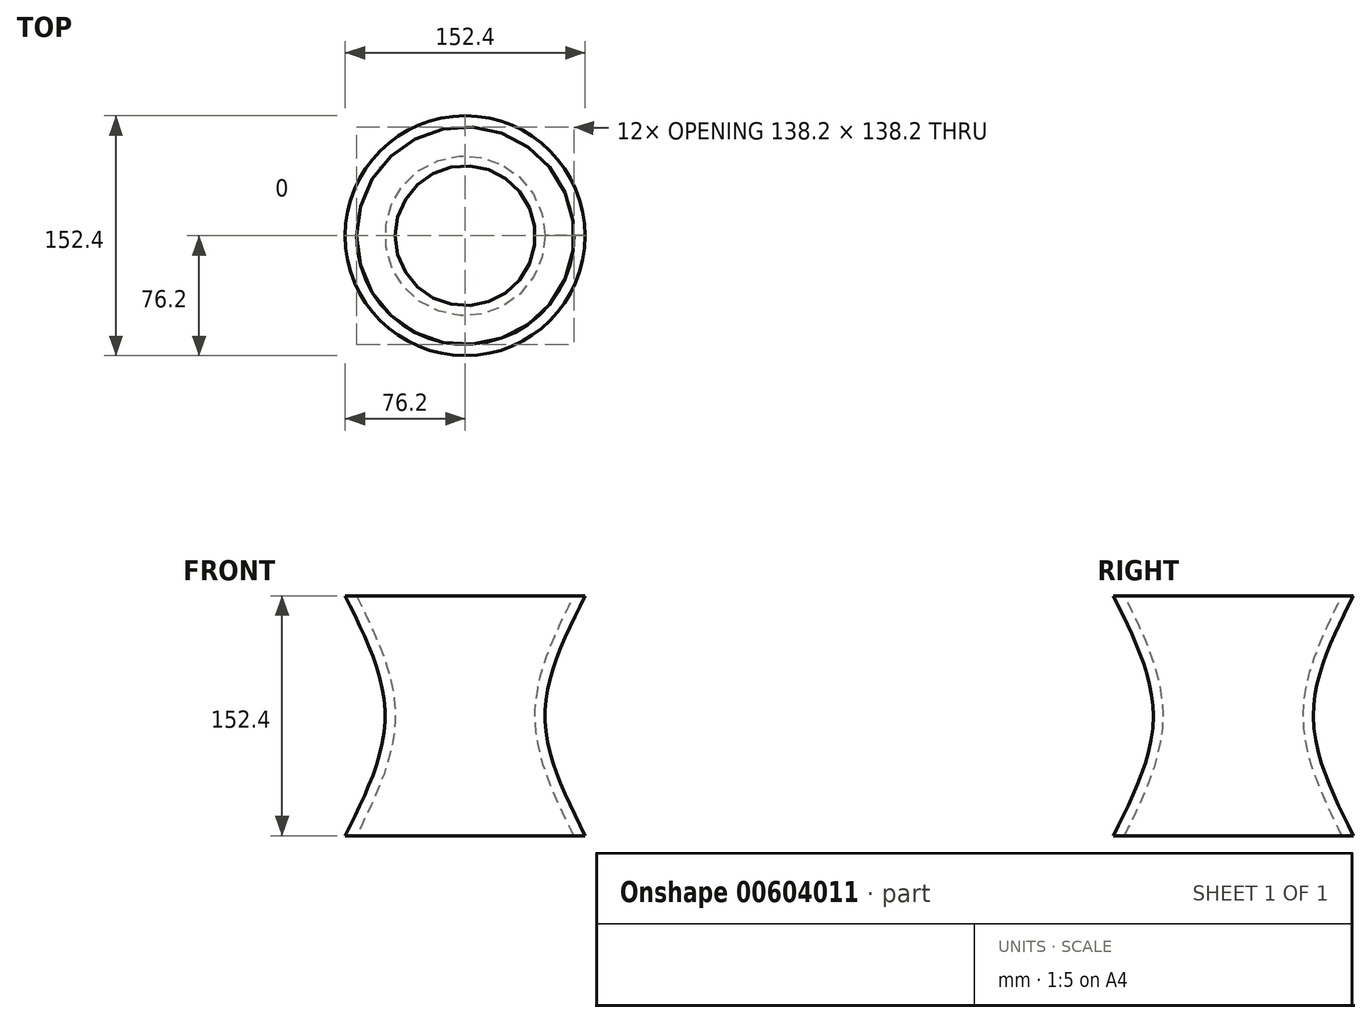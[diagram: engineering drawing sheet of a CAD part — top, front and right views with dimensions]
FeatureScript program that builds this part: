
annotation { "Feature Type Name" : "Feature", "Feature Type Description" : "" }
export const myFeature = defineFeature(function(context is Context, id is Id, definition is map)
    precondition{}
    {
        {
            var Q0;
            Q0=qCreatedBy(makeId("Top.planeOp"),FACE);
            var sketch = newSketch(context, id + "F0", { "sketchPlane" : qUnion([Q0])});
            skCircle(sketch, "E0", {"center": v(0, 0) * mm, "radius": 76.2 * mm});
            skSolve(sketch);
        }
        {
            var Q0;
            Q0=makeQuery(id+"F0.imprint","IMPRINT",FACE,{"disambiguationData":[TD([[makeQuery(id+"F0.imprint","IMPRINT",EDGE,{"derivedFrom":sQuery(id+"F0.wireOp",EDGE,"E0")}),1.0]])]});
            cPlane(context, id + "F1", {"entities" : qUnion([Q0]), "cplaneType" : CPlaneType.OFFSET, "offset" : 76.2 * mm, "width" : 152.4 * mm, "height" : 152.4 * mm});
        }
        {
            var Q0;
            Q0=qCreatedBy(id+"F1.planeOp",FACE);
            var sketch = newSketch(context, id + "F2", { "sketchPlane" : qUnion([Q0])});
            skCircle(sketch, "E1", {"center": v(0, 0) * mm, "radius": 50.8 * mm});
            skSolve(sketch);
        }
        {
            var Q0;
            Q0=makeQuery(id+"F2.imprint","IMPRINT",FACE,{"disambiguationData":[TD([[makeQuery(id+"F2.imprint","IMPRINT",EDGE,{"derivedFrom":sQuery(id+"F2.wireOp",EDGE,"E1")}),1.0]])]});
            cPlane(context, id + "F3", {"entities" : qUnion([Q0]), "cplaneType" : CPlaneType.OFFSET, "offset" : 76.2 * mm, "width" : 152.4 * mm, "height" : 152.4 * mm});
        }
        {
            var Q0;
            Q0=qCreatedBy(id+"F3.planeOp",FACE);
            var sketch = newSketch(context, id + "F4", { "sketchPlane" : qUnion([Q0])});
            skCircle(sketch, "E2", {"center": v(0, 0) * mm, "radius": 76.2 * mm});
            skSolve(sketch);
        }
        {
            var Q0;
            Q0=makeQuery(id+"F4.imprint","IMPRINT",FACE,{"disambiguationData":[TD([[makeQuery(id+"F4.imprint","IMPRINT",EDGE,{"derivedFrom":sQuery(id+"F4.wireOp",EDGE,"E2")}),1.0]])]});
            var Q1;
            Q1=makeQuery(id+"F2.imprint","IMPRINT",FACE,{"disambiguationData":[TD([[makeQuery(id+"F2.imprint","IMPRINT",EDGE,{"derivedFrom":sQuery(id+"F2.wireOp",EDGE,"E1")}),1.0]])]});
            var Q2;
            Q2=makeQuery(id+"F0.imprint","IMPRINT",FACE,{"disambiguationData":[TD([[makeQuery(id+"F0.imprint","IMPRINT",EDGE,{"derivedFrom":sQuery(id+"F0.wireOp",EDGE,"E0")}),1.0]])]});
            loft(context, id + "F5", {"sheetProfilesArray" : [{ "sheetProfileEntities" : qUnion([Q0]) }, { "sheetProfileEntities" : qUnion([Q1]) }, { "sheetProfileEntities" : qUnion([Q2]) }]});
        }
        {
            var Q0;
            Q0=makeQuery(id+"F5.opLoft","CAP_FACE",FACE,{"disambiguationData":[OSD([makeQuery(id+"F4.imprint","IMPRINT",FACE,{"disambiguationData":[TD([[makeQuery(id+"F4.imprint","IMPRINT",EDGE,{"derivedFrom":sQuery(id+"F4.wireOp",EDGE,"E2")}),1.0]])]})])],"isStart":true});
            var Q1;
            Q1=makeQuery(id+"F5.opLoft","CAP_FACE",FACE,{"disambiguationData":[OSD([makeQuery(id+"F0.imprint","IMPRINT",FACE,{"disambiguationData":[TD([[makeQuery(id+"F0.imprint","IMPRINT",EDGE,{"derivedFrom":sQuery(id+"F0.wireOp",EDGE,"E0")}),1.0]])]})])],"isStart":true});
            shell(context, id + "F6", {"entities" : qUnion([Q0, Q1]), "thickness" : 6.35 * mm});
        }
    });
